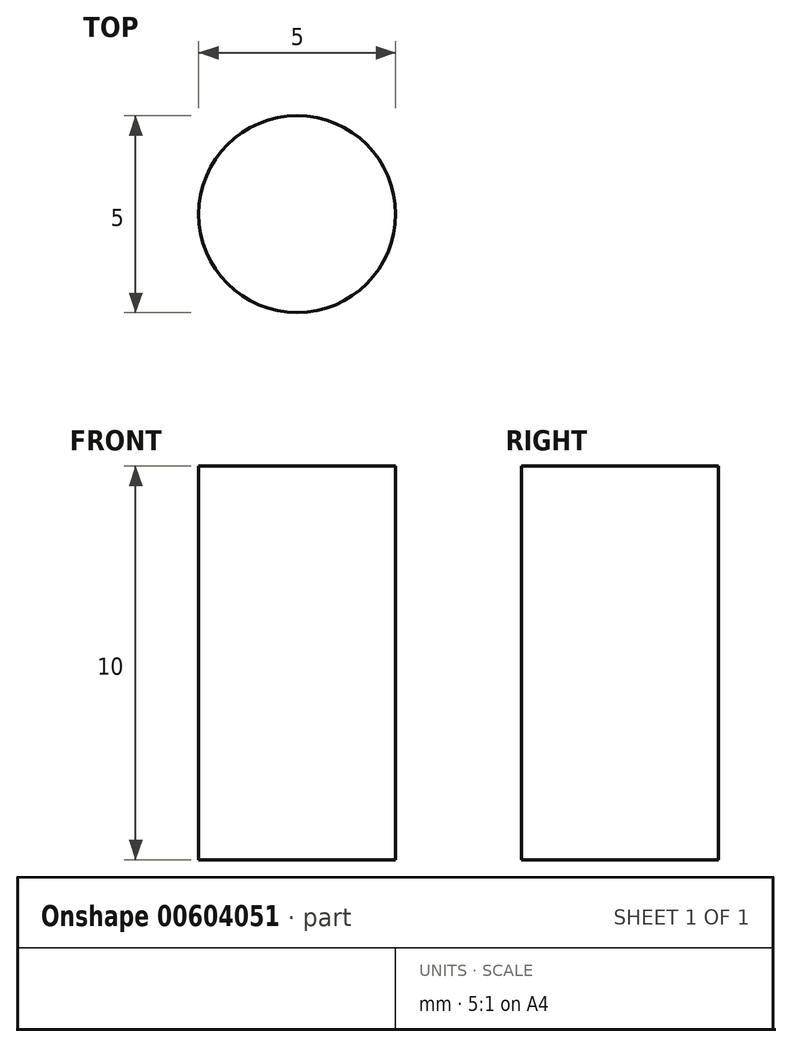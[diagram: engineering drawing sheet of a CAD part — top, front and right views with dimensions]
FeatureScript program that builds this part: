
annotation { "Feature Type Name" : "Feature", "Feature Type Description" : "" }
export const myFeature = defineFeature(function(context is Context, id is Id, definition is map)
    precondition{}
    {
        {
            var Q0;
            Q0=qCreatedBy(makeId("Front.planeOp"),FACE);
            var sketch = newSketch(context, id + "F0", { "sketchPlane" : qUnion([Q0])});
            skLineSegment(sketch, "E0", {"start": v(0, 0) * mm, "end": v(3.5, 0) * mm});
            skLineSegment(sketch, "E1", {"start": v(3.5, 0) * mm, "end": v(5, -4) * mm});
            skLineSegment(sketch, "E2", {"start": v(5, -4) * mm, "end": v(5, -10) * mm});
            skArc(sketch, "E3", {"start": v(5, -10) * mm, "mid": v(7.93, -17.07) * mm, "end": v(15, -20) * mm});
            skLineSegment(sketch, "E4.left", {"start": v(15, -20) * mm, "end": v(15, -27) * mm});
            skLineSegment(sketch, "E5", {"start": v(15, -27) * mm, "end": v(13, -27) * mm});
            skLineSegment(sketch, "E6", {"start": v(13, -27) * mm, "end": v(13, -30) * mm});
            skLineSegment(sketch, "E7", {"start": v(13, -30) * mm, "end": v(15, -30) * mm});
            skLineSegment(sketch, "E8", {"start": v(15, -30) * mm, "end": v(15, -35) * mm});
            skLineSegment(sketch, "E9", {"start": v(15, -35) * mm, "end": v(13, -35) * mm});
            skLineSegment(sketch, "E10", {"start": v(13, -35) * mm, "end": v(13, -37) * mm});
            skLineSegment(sketch, "E11", {"start": v(13, -37) * mm, "end": v(15, -37) * mm});
            skLineSegment(sketch, "E12", {"start": v(15, -37) * mm, "end": v(15, -40) * mm});
            skLineSegment(sketch, "E13", {"start": v(15, -40) * mm, "end": v(20, -40) * mm});
            skLineSegment(sketch, "E14", {"start": v(20, -40) * mm, "end": v(20, -50) * mm});
            skLineSegment(sketch, "E15", {"start": v(20, -50) * mm, "end": v(0, -50) * mm});
            skLineSegment(sketch, "E16", {"start": v(0, -50) * mm, "end": v(0, 0) * mm});
            skLineSegment(sketch, "E17.bottom", {"start": v(0, 0) * mm, "end": v(2.5, 0) * mm});
            skLineSegment(sketch, "E17.top", {"start": v(0, -10) * mm, "end": v(2.5, -10) * mm});
            skLineSegment(sketch, "E17.left", {"start": v(0, 0) * mm, "end": v(0, -10) * mm});
            skLineSegment(sketch, "E17.right", {"start": v(2.5, 0) * mm, "end": v(2.5, -10) * mm});
            skLineSegment(sketch, "E18", {"start": v(2.5, -10) * mm, "end": v(2, -12) * mm});
            skLineSegment(sketch, "E19", {"start": v(2, -12) * mm, "end": v(0, -12) * mm});
            skLineSegment(sketch, "E20", {"start": v(0, -12) * mm, "end": v(0, -10) * mm});
            skSolve(sketch);
        }
        {
            var Q0;
            Q0=makeQuery(id+"F0.imprint","IMPRINT",FACE,{"disambiguationData":[TD([[makeQuery(id+"F0.imprint","IMPRINT",EDGE,{"derivedFrom":sQuery(id+"F0.wireOp",EDGE,"E0")}),-1.0]])]});
            var Q1;
            Q1=sQuery(id+"F0.wireOp",EDGE,"E16");
            revolve(context, id + "F1", {"entities" : qUnion([Q0]), "axis" : qUnion([Q1]), "revolveType" : RevolveType.FULL});
        }
    });
